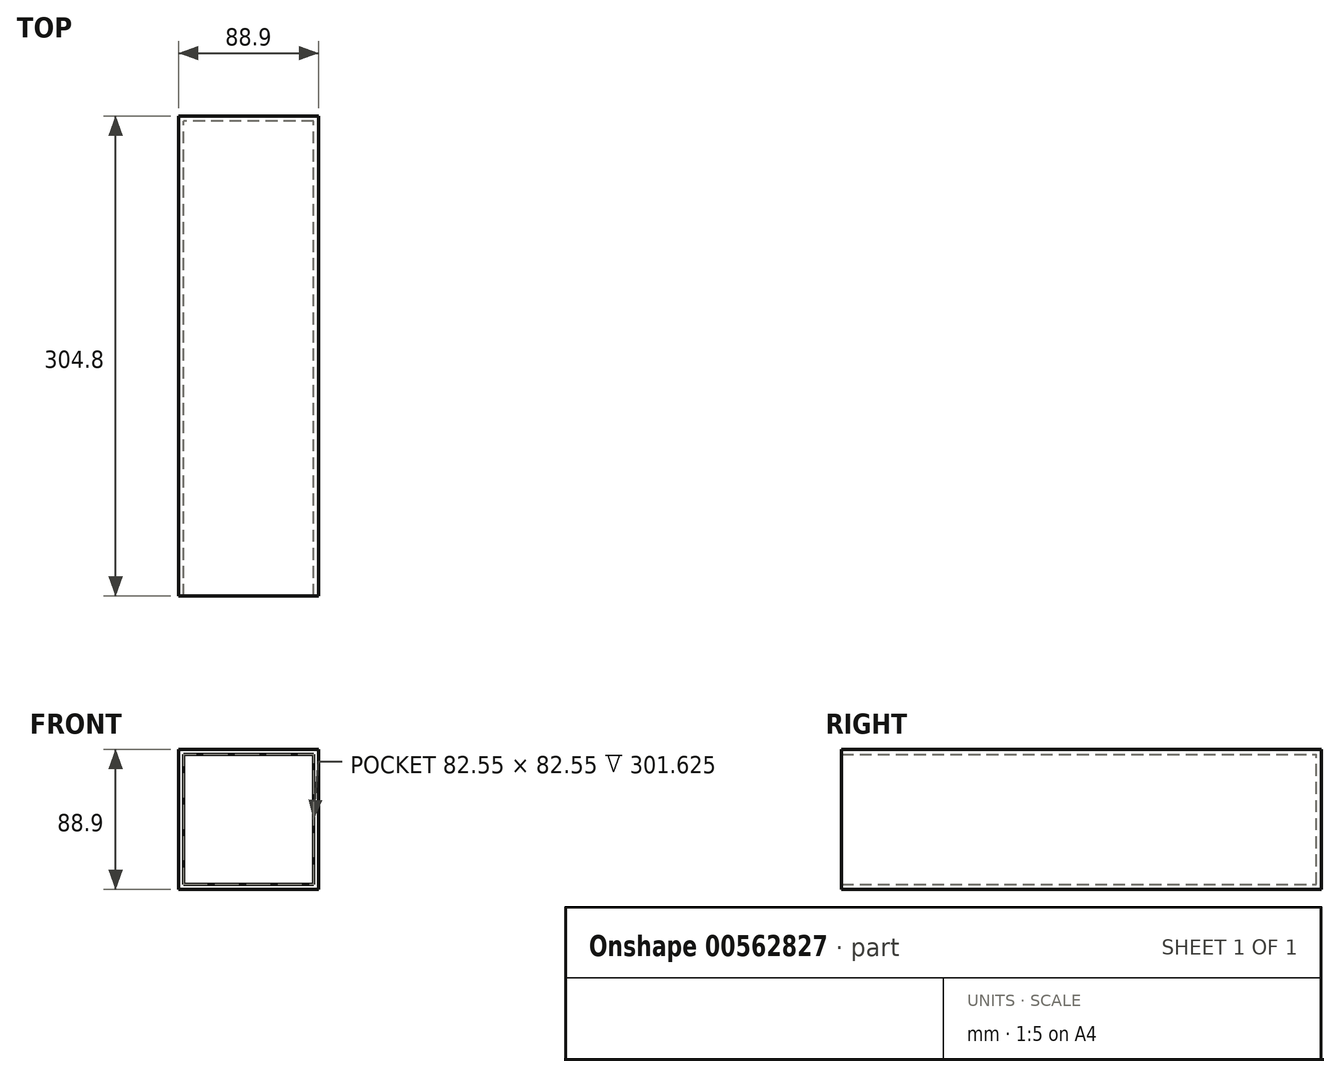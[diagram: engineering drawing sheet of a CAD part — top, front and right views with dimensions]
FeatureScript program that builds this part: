
annotation { "Feature Type Name" : "Feature", "Feature Type Description" : "" }
export const myFeature = defineFeature(function(context is Context, id is Id, definition is map)
    precondition{}
    {
        {
            var Q0;
            Q0=qCreatedBy(makeId("Front.planeOp"),FACE);
            var sketch = newSketch(context, id + "F0", { "sketchPlane" : qUnion([Q0])});
            skLineSegment(sketch, "E0.bottom", {"start": v(44.45, -44.45) * mm, "end": v(-44.45, -44.45) * mm});
            skLineSegment(sketch, "E0.top", {"start": v(44.45, 44.45) * mm, "end": v(-44.45, 44.45) * mm});
            skLineSegment(sketch, "E0.left", {"start": v(44.45, -44.45) * mm, "end": v(44.45, 44.45) * mm});
            skLineSegment(sketch, "E0.right", {"start": v(-44.45, -44.45) * mm, "end": v(-44.45, 44.45) * mm});
            skPoint(sketch, "E0.middle", {"position": v(0, 0) * mm});
            skSolve(sketch);
        }
        {
            var Q0;
            Q0=qSketchRegion(id+"F0",true);
            extrude(context, id + "F1", {"entities" : qUnion([Q0]), "depth" : 304.8 * mm, "offsetDistance" : 25.4 * mm});
        }
        {
            var Q0;
            Q0=makeQuery(id+"F1.opExtrude","CAP_FACE",FACE,{"disambiguationData":[OSD([sQuery(id+"F0.wireOp",EDGE,"E0.bottom"),sQuery(id+"F0.wireOp",EDGE,"E0.top"),sQuery(id+"F0.wireOp",EDGE,"E0.left"),sQuery(id+"F0.wireOp",EDGE,"E0.right")])],"isStart":false});
            shell(context, id + "F2", {"entities" : qUnion([Q0]), "thickness" : 3.17 * mm});
        }
    });
